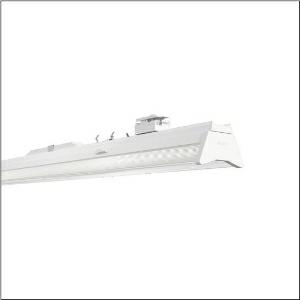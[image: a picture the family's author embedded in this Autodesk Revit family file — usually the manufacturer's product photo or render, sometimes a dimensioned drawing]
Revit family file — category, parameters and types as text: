
# Revit family: licross_r__11_performance_ho_51td16mn4gxm_b838
name_source: partatom
category: Lighting Fixtures
units: mm (PartAtom-declared; Revit-internal decimal feet)

## family parameters
Cut with Voids When Loaded = No
Host = Face
Light Source = No
Part Type = Normal
Room Calculation Point = No
Round Connector Dimension = Use Diameter
Shared = No

## types (1)
- --- (1 x LED, 16020 lm, 87.4 W, 4000K)
    Apparent Load = 87 VA
    CIE Flux Codes = 63 87 95 78 100
    Color Rendering = 80
    Color Temperature = 4000K
    Default Elevation = 1800 mm
    Description = Licross® 11 Performance HO, luminaire insert, of sheet steel, galvanised, coil coated, white, length: 1.500mm, width: 120mm, height: 123mm, LED rated luminous flux: 16.020lm, light colour: 840, control gear: ON/OFF Multilumen, with plug, 3-pole, with phase selection, mains connection: 220..240V, AC, 50/60Hz, rated input power: 87W, internal wiring halogen-free, primary light control with lens, of plastic, primary optical cover: cover, of PMMA, light emission: direct/indirect distribution, primary light characteristic: symmetric, protection rating (complete): IP54, insulation class (complete): insulation class I (protective earthing), certification: CE, ENEC, VDE, UKCA, protection symbol: D if used in an environment with non-conductive dust loads with corresponding accessories, impact resistance: IK06, permissible ambient temperature for indoor applications: -35..+35°C, corresponds to IFS (International Featured Standards) requirements for safety and quality in the food industry, reducing of maximum allowable ambient temperature of 5°C with ceiling mounting, LABS conformity tested according to VDMA 24364:2018-05, packaging unit: 1 piece
    Height = 114 mm
    Lamp = 1 x LED
    Lamp Light Flux = 16020 lm
    Lamp Power = 87.4 W
    Lamp count = 1
    Length = 1500 mm
    Luminous efficacy = 183 lm/W
    Manufacturer = Siteco
    ModVariant = No
    Model = 51TD16MN4GXM
    Mounting Place = Ceiling
    Mounting Type = Pendant
    Number of Poles = 1
    OnlyDefault = Yes
    Power Factor = 1
    Product Name = Licross® 11 Performance HO
    Product group = luminaire insert | ceiling pendant
    ProductGroupID = 902
    Protection Class = Protection class I
    Protection Degree = IP 54
    RLX_Detail_Level = 1
    RLX_Emergency_Light_Flux = 0 lm
    RLX_Emergency_Type = 0
    RLX_Emergency_Type_DB = No
    RlxData = <blob elided: 31809 chars, md5=293479d0>
    Socket = socket
    Standby Power = 0 W
    System Light Flux = 16020 lm
    System Power = 87 W
    Type Comments = factory setting: luminous flux: 100 % | (A | C | E) | 203 mA
    Type Image = l_1256138.jpg
    URL = http://relux.com
    VarID = @adj_107729
    Voltage = 0 V
    Weight = 0.00 kg
    Width = 120 mm

## geometry (parser evidence)
native form markers: Blend x4, Sweep x12
no freeform markers — native parametric forms only
